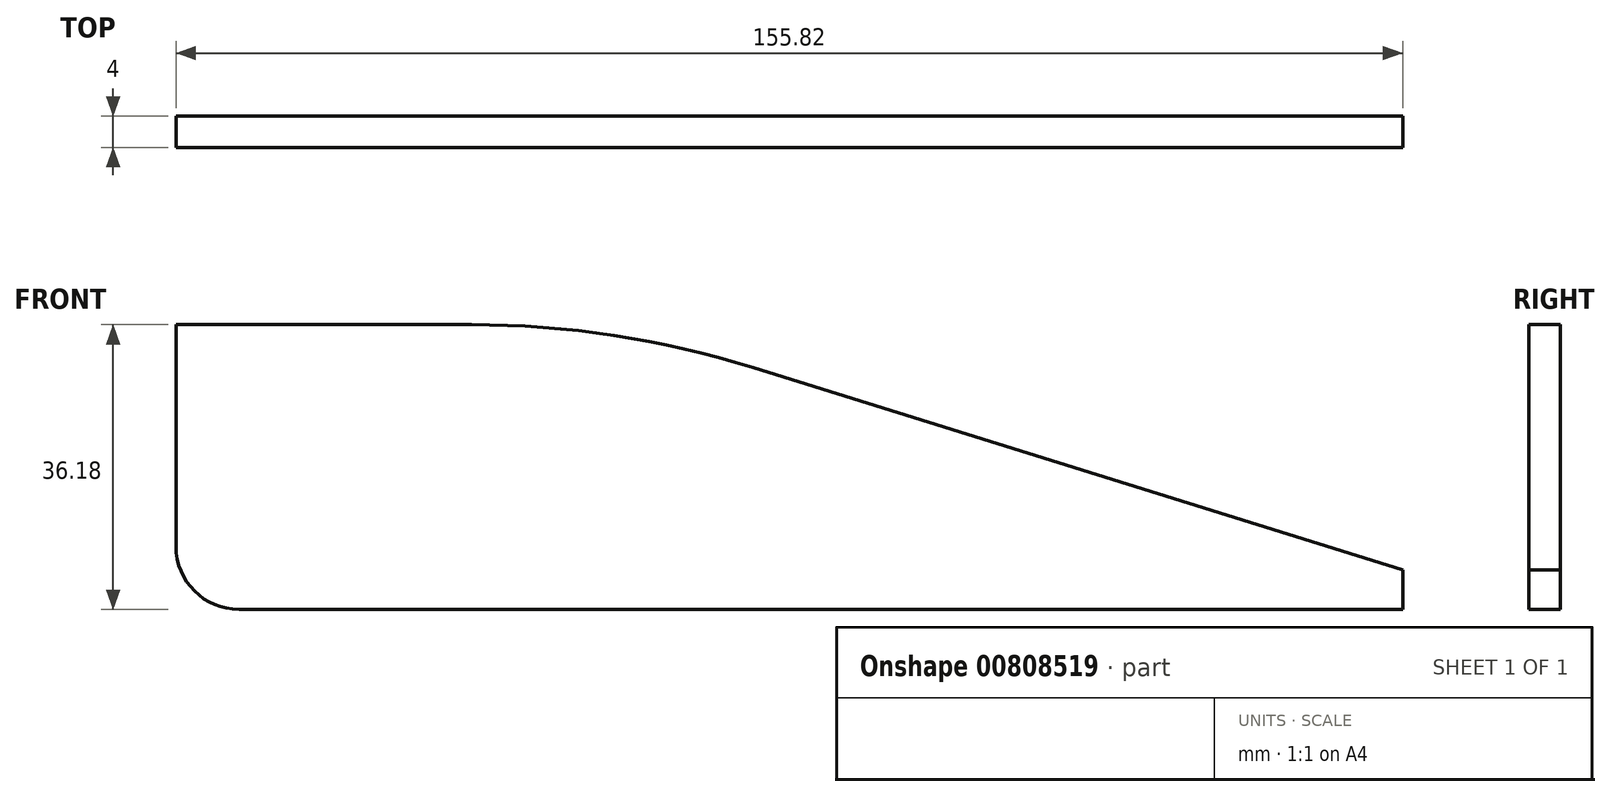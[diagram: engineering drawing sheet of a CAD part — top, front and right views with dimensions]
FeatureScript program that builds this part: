
annotation { "Feature Type Name" : "Feature", "Feature Type Description" : "" }
export const myFeature = defineFeature(function(context is Context, id is Id, definition is map)
    precondition{}
    {
        {
            var Q0;
            Q0=qCreatedBy(makeId("Front.planeOp"),FACE);
            var sketch = newSketch(context, id + "F0", { "sketchPlane" : qUnion([Q0])});
            skLineSegment(sketch, "E0", {"start": v(-155.82, 40.23) * mm, "end": v(-155.82, 12.05) * mm});
            skLineSegment(sketch, "E1", {"start": v(-147.82, 4.05) * mm, "end": v(0, 4.05) * mm});
            skLineSegment(sketch, "E2", {"start": v(-155.82, 40.23) * mm, "end": v(-118.27, 40.23) * mm});
            skLineSegment(sketch, "E3", {"start": v(0, 4.05) * mm, "end": v(0, 9.05) * mm});
            skLineSegment(sketch, "E4", {"start": v(0, 9.05) * mm, "end": v(-82.56, 34.79) * mm});
            skPoint(sketch, "E5.visualSharp", {"position": v(-100, 40.23) * mm});
            skArc(sketch, "E5.filletArc", {"start": v(-82.56, 34.79) * mm, "mid": v(-100.2, 38.86) * mm, "end": v(-118.27, 40.23) * mm});
            skPoint(sketch, "E6.visualSharp", {"position": v(-155.82, 4.05) * mm});
            skArc(sketch, "E6.filletArc", {"start": v(-155.82, 12.05) * mm, "mid": v(-153.47, 6.4) * mm, "end": v(-147.82, 4.05) * mm});
            skLineSegment(sketch, "E7", {"start": v(0, 6.55) * mm, "end": v(-153.47, 6.4) * mm, "construction": true});
            skSolve(sketch);
        }
        {
            var Q0;
            Q0=makeQuery(id+"F0.imprint","IMPRINT",FACE,{"disambiguationData":[TD([[makeQuery(id+"F0.imprint","IMPRINT",EDGE,{"derivedFrom":sQuery(id+"F0.wireOp",EDGE,"E0")}),1.0]])]});
            extrude(context, id + "F1", {"entities" : qUnion([Q0]), "depth" : 4 * mm, "offsetDistance" : 25 * mm});
        }
    });
